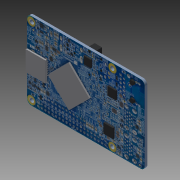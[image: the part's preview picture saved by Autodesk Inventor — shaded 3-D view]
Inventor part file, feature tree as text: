
AUTODESK INVENTOR PART (.ipt)
format: ipt  version: 2013 SP2 (Build 170200200, 200)  size: 244,224 bytes
history: native  units: mm
features: sketch x6, extrude x5, fillet x1, hole x1
ambient origin geometry x8: Origin, YZ Plane, XZ Plane, XY Plane, X Axis, Y Axis, Z Axis, Center Point
bodies: Solid1 (feature_tree)
feature tree (13):
  extrude  "Extrusion1"  Depth=56.0mm
  fillet  "Fillet1"  Radius=1.8mm
  hole  "Hole1"  [1 undecoded]
  extrude  "Extrusion2"  Depth=3.5mm
  extrude  "Extrusion3"  Depth=3.5mm
  extrude  "Extrusion4"  Depth=3.5mm
  extrude  "Extrusion5"  Depth=1.0mm TaperAngle=0.0deg
  sketch  "Sketch1"  dims[d0=85.0mm d1=56.0mm d2=1.8mm d3=0.0mm]
  sketch  "Sketch2"  dims[d4=3.0mm d5=58.0mm]
  sketch  "Sketch3"  dims[d7=49.0mm d8=3.5mm]
  sketch  "Sketch4"  dims[d9=3.5mm d10=3.5mm]
  sketch  "Sketch5"  dims[d11=3.5mm d12=3.5mm]
  sketch  "Sketch6"  dims[d13=3.5mm d14=3.0mm d15=6.0mm d16=4.0mm d17=2.0mm d18=90.0deg d19=8.0mm d20=20.594885mm d21=1.0mm d22=0.0mm d23=1.0mm d24=0.0mm d25=0.0mm d27=3.0mm d28=0.0mm d29=5.0mm d30=0.0mm]
note: 1 required parameter value undecoded (feature->parameter linkage not recoverable at this tier; creation-order binding heuristic only, values carry confidence <= 0.55)
